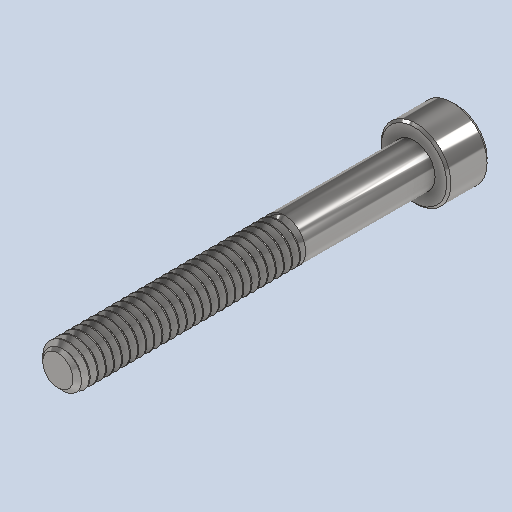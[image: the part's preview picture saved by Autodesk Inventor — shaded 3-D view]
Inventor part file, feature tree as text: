
AUTODESK INVENTOR PART (.ipt)
format: ipt  version: 2023 (Build 270158000, 158)  size: 711,168 bytes
history: native  units: in
note: dims shown in document units (in); Inventor stores cm internally (conversion verified against a paired STEP export)
features: chamfer x1
ambient origin geometry x8: Origin, YZ Plane, XZ Plane, XY Plane, X Axis, Y Axis, Z Axis, Center Point
bodies: Solid1 (feature_tree)
feature tree (1):
  chamfer  "Chamfer2"  [1 undecoded]
note: 1 required parameter value undecoded (feature->parameter linkage not recoverable at this tier; creation-order binding heuristic only, values carry confidence <= 0.55)
